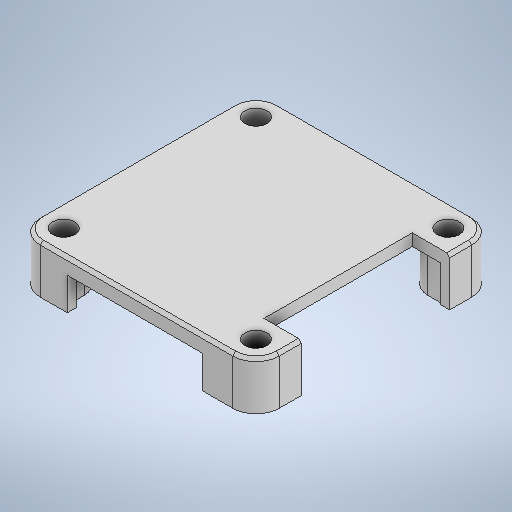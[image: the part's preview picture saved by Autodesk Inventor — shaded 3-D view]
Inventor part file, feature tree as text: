
AUTODESK INVENTOR PART (.ipt)
format: ipt  version: 2025.2 (Build 292293000, 293)  size: 792,064 bytes
history: native  units: mm
features: sketch x10, extrude x8, projected_geometry x6, chamfer x1
ambient origin geometry x8: Origin, YZ Plane, XZ Plane, XY Plane, X Axis, Y Axis, Z Axis, Center Point
bodies: Solid1 (feature_tree)
feature tree (25):
  extrude  "Extrusion1"  Depth=3.15mm
  extrude  "Extrusion2"  Depth=7.0mm TaperAngle=0.0deg
  extrude  "Extrusion3"  Depth=20.05mm
  extrude  "Extrusion4"  Depth=1.2mm
  extrude  "Extrusion5"  Depth=6.5mm
  extrude  "Extrusion6"  Depth=6.8mm
  extrude  "Extrusion8"  Depth=18.35mm
  extrude  "Extrusion9"  Depth=4.4mm TaperAngle=0.0deg
  sketch  "Sketch11"  dims[d41=26.0mm d42=26.0mm d44=1.1mm d45=0.0mm d46=0.5mm d47=0.0mm d48=5.5mm d49=26.0mm d50=26.0mm d51=0.4mm d52=2.0mm d53=45.0deg]
  chamfer  "Chamfer2"  [1 undecoded]
  sketch  "Sketch1"  dims[d0=32.3mm d1=3.15mm]
  sketch  "Sketch Circular Pattern1"  dims[d2=40.0mm d4=360.0deg d6=7.0mm d7=0.0mm]
  sketch  "Sketch2"  dims[d8=5.05mm d10=20.05mm]
  projected_geometry  "Projected Loop1"
  sketch  "Sketch4"  dims[d11=0.0mm d12=0.0mm d13=1.2mm]
  sketch  "Sketch5"  dims[d14=6.0mm d15=0.0mm d16=6.5mm]
  projected_geometry  "Projected Loop2"
  sketch  "Sketch6"  dims[d17=19.2mm d18=6.8mm]
  sketch  "Sketch7"  dims[d19=18.3mm d20=18.35mm]
  sketch  "Sketch9"  dims[d21=4.4mm d22=0.0mm d27=4.4mm d28=0.0mm]
  projected_geometry  "Projected Loop4"
  sketch  "Sketch10"  dims[d31=3.0mm d32=0.0mm d33=0.0mm]
  projected_geometry  "Projected Loop5"
  projected_geometry  "Projected Loop6"
  projected_geometry  "Projected Loop7"
note: 1 required parameter value undecoded (feature->parameter linkage not recoverable at this tier; creation-order binding heuristic only, values carry confidence <= 0.55)
